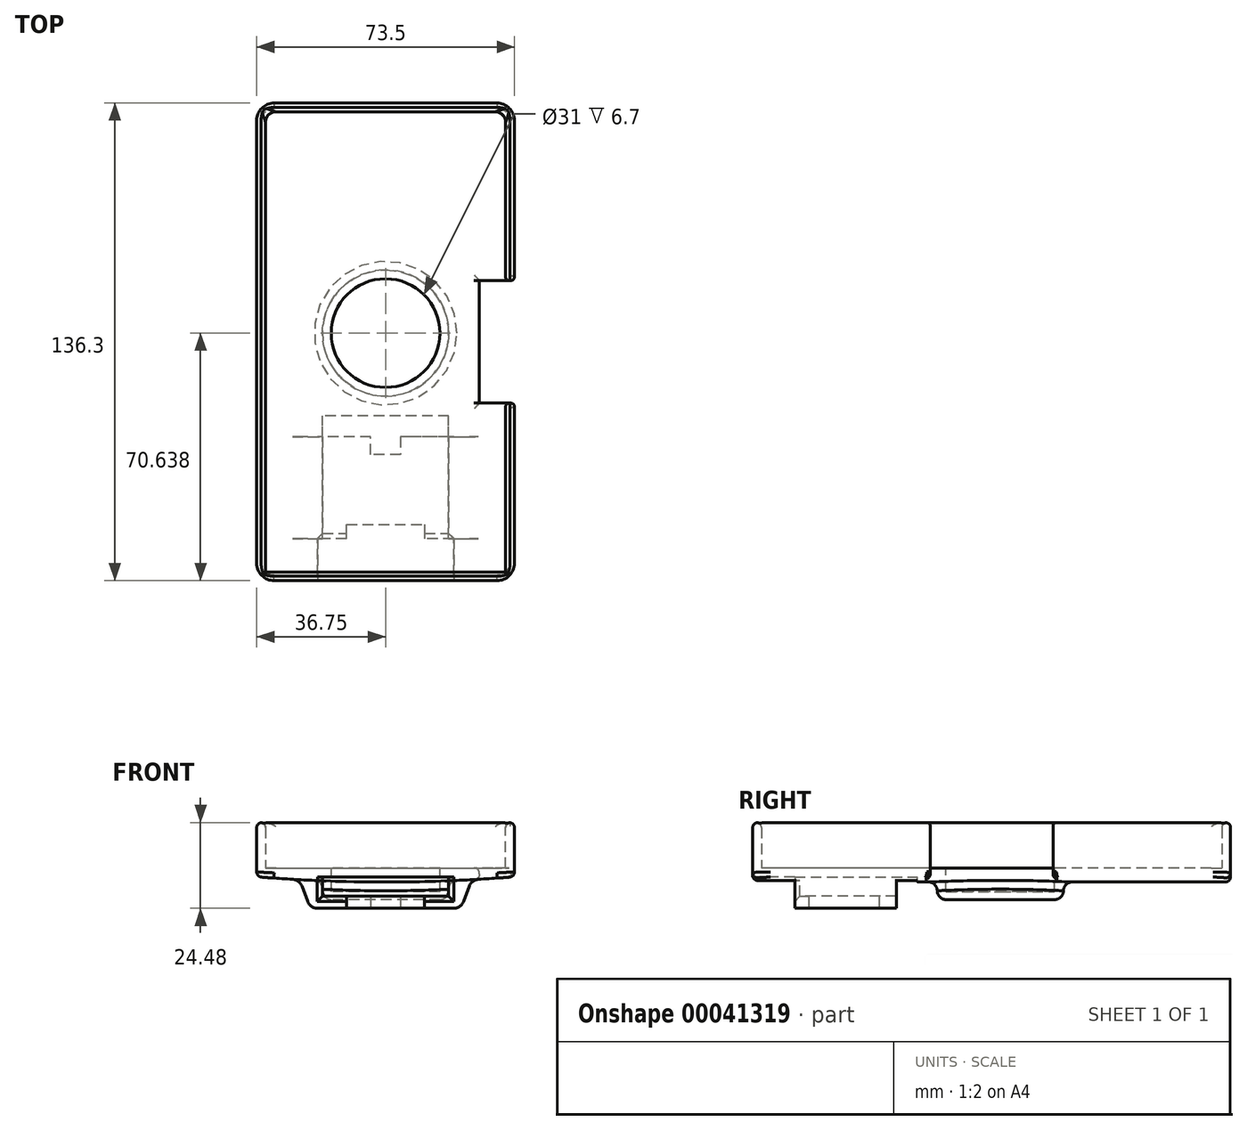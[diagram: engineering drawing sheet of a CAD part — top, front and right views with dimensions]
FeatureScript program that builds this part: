
annotation { "Feature Type Name" : "Feature", "Feature Type Description" : "" }
export const myFeature = defineFeature(function(context is Context, id is Id, definition is map)
    precondition{}
    {
        {
            var Q0;
            Q0=qCreatedBy(makeId("Top.planeOp"),FACE);
            var sketch = newSketch(context, id + "F0", { "sketchPlane" : qUnion([Q0])});
            skLineSegment(sketch, "E0.bottom", {"start": v(-33.25, 64.65) * mm, "end": v(33.25, 64.65) * mm, "construction": true});
            skLineSegment(sketch, "E0.top", {"start": v(-33.25, -64.65) * mm, "end": v(33.25, -64.65) * mm, "construction": true});
            skLineSegment(sketch, "E0.left", {"start": v(-33.25, 64.65) * mm, "end": v(-33.25, -64.65) * mm, "construction": true});
            skLineSegment(sketch, "E0.right", {"start": v(33.25, 64.65) * mm, "end": v(33.25, 14.65) * mm, "construction": true});
            skLineSegment(sketch, "E1", {"start": v(33.25, 14.65) * mm, "end": v(28.25, 14.65) * mm, "construction": true});
            skLineSegment(sketch, "E2", {"start": v(28.25, 14.65) * mm, "end": v(28.25, -14.65) * mm, "construction": true});
            skLineSegment(sketch, "E3", {"start": v(28.25, -14.65) * mm, "end": v(33.25, -14.65) * mm, "construction": true});
            skLineSegment(sketch, "E4.trimOffspring", {"start": v(33.25, -14.65) * mm, "end": v(33.25, -64.65) * mm, "construction": true});
            skCircle(sketch, "E5", {"center": v(-0.75, 2.65) * mm, "radius": 20.34 * mm, "construction": true});
            skSolve(sketch);
        }
        {
            var Q0;
            Q0=qCreatedBy(makeId("Top.planeOp"),FACE);
            var sketch = newSketch(context, id + "F1", { "sketchPlane" : qUnion([Q0])});
            skLineSegment(sketch, "E6.bottom", {"start": v(-34.25, 65.65) * mm, "end": v(34.25, 65.65) * mm, "construction": true});
            skLineSegment(sketch, "E6.top", {"start": v(-34.25, -65.65) * mm, "end": v(34.25, -65.65) * mm, "construction": true});
            skLineSegment(sketch, "E6.left", {"start": v(-34.25, 65.65) * mm, "end": v(-34.25, -65.65) * mm, "construction": true});
            skLineSegment(sketch, "E6.right", {"start": v(34.25, 65.65) * mm, "end": v(34.25, -65.65) * mm, "construction": true});
            skLineSegment(sketch, "E7.0", {"start": v(-36.75, 68.15) * mm, "end": v(36.75, 68.15) * mm});
            skLineSegment(sketch, "E7.1", {"start": v(-36.75, 68.15) * mm, "end": v(-36.75, -68.15) * mm});
            skLineSegment(sketch, "E7.2", {"start": v(-36.75, -68.15) * mm, "end": v(36.75, -68.15) * mm});
            skLineSegment(sketch, "E7.3", {"start": v(36.75, 68.15) * mm, "end": v(36.75, -68.15) * mm});
            skSolve(sketch);
        }
        {
            var Q0;
            Q0 = qSketchRegion(id + "F1", true);
            extrude(context, id + "F2", {"entities" : qUnion([Q0]), "depth" : 2.5 * mm});
        }
        {
            var Q0;
            Q0=makeQuery(id+"F2.opExtrude","CAP_FACE",FACE,{"disambiguationData":[OSD([sQuery(id+"F1.wireOp",EDGE,"E7.0"),sQuery(id+"F1.wireOp",EDGE,"E7.1"),sQuery(id+"F1.wireOp",EDGE,"E7.2"),sQuery(id+"F1.wireOp",EDGE,"E7.3")])],"isStart":false});
            var sketch = newSketch(context, id + "F3", { "sketchPlane" : qUnion([Q0])});
            skLineSegment(sketch, "E8.bottom", {"start": v(-36.75, 68.15) * mm, "end": v(36.75, 68.15) * mm});
            skLineSegment(sketch, "E8.top", {"start": v(-36.75, -68.15) * mm, "end": v(36.75, -68.15) * mm});
            skLineSegment(sketch, "E8.left", {"start": v(-36.75, 68.15) * mm, "end": v(-36.75, -68.15) * mm});
            skLineSegment(sketch, "E8.right", {"start": v(36.75, 68.15) * mm, "end": v(36.75, -68.15) * mm});
            skLineSegment(sketch, "E9.0", {"start": v(-34.25, 65.65) * mm, "end": v(34.25, 65.65) * mm});
            skLineSegment(sketch, "E9.1", {"start": v(-34.25, 65.65) * mm, "end": v(-34.25, -65.65) * mm});
            skLineSegment(sketch, "E9.2", {"start": v(-34.25, -65.65) * mm, "end": v(34.25, -65.65) * mm});
            skLineSegment(sketch, "E9.3", {"start": v(34.25, 65.65) * mm, "end": v(34.25, -65.65) * mm});
            skSolve(sketch);
        }
        {
            var Q0;
            Q0 = qSketchRegion(id + "F3", true);
            extrude(context, id + "F4", {"entities" : qUnion([Q0]), "operationType" : NewBodyOperationType.ADD, "depth" : 13 * mm});
        }
        {
            var Q0;
            Q0=makeQuery(id+"F4.boolean.opBoolean","MERGE",FACE,{"derivedFrom":[makeQuery(id+"F2.opExtrude","SWEPT_FACE",FACE,{"disambiguationData":[OSD([sQuery(id+"F1.wireOp",EDGE,"E7.0")])]}),makeQuery(id+"F4.opExtrude","SWEPT_FACE",FACE,{"disambiguationData":[OSD([sQuery(id+"F3.wireOp",EDGE,"E8.bottom")])]})]});
            var sketch = newSketch(context, id + "F5", { "sketchPlane" : qUnion([Q0])});
            skLineSegment(sketch, "E10", {"start": v(-46.23, -1.5) * mm, "end": v(62.2, -1.5) * mm, "construction": true});
            skPoint(sketch, "E11", {"position": v(0, -1.5) * mm});
            skArc(sketch, "E12", {"start": v(-36.75, 0) * mm, "mid": v(0, -1.5) * mm, "end": v(36.75, 0) * mm});
            skPoint(sketch, "E12.first.point", {"position": v(-36.75, 0) * mm});
            skPoint(sketch, "E12.second.point", {"position": v(36.75, 0) * mm});
            skLineSegment(sketch, "E13", {"start": v(36.75, 0) * mm, "end": v(-36.75, 0) * mm});
            skSolve(sketch);
        }
        {
            var Q0;
            Q0 = qSketchRegion(id + "F5", true);
            var Q1;
            Q1=makeQuery(id+"F4.boolean.opBoolean","MERGE",FACE,{"derivedFrom":[makeQuery(id+"F2.opExtrude","SWEPT_FACE",FACE,{"disambiguationData":[OSD([sQuery(id+"F1.wireOp",EDGE,"E7.2")])]}),makeQuery(id+"F4.opExtrude","SWEPT_FACE",FACE,{"disambiguationData":[OSD([sQuery(id+"F3.wireOp",EDGE,"E8.top")])]})]});
            extrude(context, id + "F6", {"entities" : qUnion([Q0]), "operationType" : NewBodyOperationType.ADD, "endBound" : BoundingType.UP_TO_SURFACE, "oppositeDirection" : true, "endBoundEntityFace" : qUnion([Q1]), "depth" : 25 * mm});
        }
        {
            var Q0;
            Q0=makeQuery(id+"F2.opExtrude","CAP_FACE",FACE,{"disambiguationData":[OSD([sQuery(id+"F1.wireOp",EDGE,"E7.0"),sQuery(id+"F1.wireOp",EDGE,"E7.1"),sQuery(id+"F1.wireOp",EDGE,"E7.2"),sQuery(id+"F1.wireOp",EDGE,"E7.3")])],"isStart":false});
            var sketch = newSketch(context, id + "F7", { "sketchPlane" : qUnion([Q0])});
            skCircle(sketch, "E14", {"center": v(0, 2.49) * mm, "radius": 15.5 * mm});
            skSolve(sketch);
        }
        {
            var Q0;
            Q0 = qSketchRegion(id + "F7", true);
            extrude(context, id + "F8", {"entities" : qUnion([Q0]), "operationType" : NewBodyOperationType.REMOVE, "endBound" : BoundingType.THROUGH_ALL, "oppositeDirection" : true, "depth" : 25 * mm});
        }
        {
            var Q0;
            Q0=qCreatedBy(makeId("Top.planeOp"),FACE);
            var sketch = newSketch(context, id + "F9", { "sketchPlane" : qUnion([Q0])});
            skCircle(sketch, "E15", {"center": v(0, 2.49) * mm, "radius": 18 * mm});
            skSolve(sketch);
        }
        {
            var Q0;
            Q0 = qSketchRegion(id + "F9", true);
            extrude(context, id + "F10", {"entities" : qUnion([Q0]), "operationType" : NewBodyOperationType.ADD, "oppositeDirection" : true, "depth" : 6.5 * mm});
        }
        {
            var Q0;
            Q0=makeQuery(id+"F2.opExtrude","CAP_FACE",FACE,{"disambiguationData":[OSD([sQuery(id+"F1.wireOp",EDGE,"E7.0"),sQuery(id+"F1.wireOp",EDGE,"E7.1"),sQuery(id+"F1.wireOp",EDGE,"E7.2"),sQuery(id+"F1.wireOp",EDGE,"E7.3")])],"isStart":false});
            var sketch = newSketch(context, id + "F11", { "sketchPlane" : qUnion([Q0])});
            skCircle(sketch, "E16", {"center": v(0, 2.49) * mm, "radius": 15.5 * mm});
            skSolve(sketch);
        }
        {
            var Q0;
            Q0 = qSketchRegion(id + "F11", true);
            extrude(context, id + "F12", {"entities" : qUnion([Q0]), "operationType" : NewBodyOperationType.REMOVE, "oppositeDirection" : true, "depth" : 6.7 * mm});
        }
        {
            var Q0;
            Q0=makeQuery(id+"F4.boolean.opBoolean","MERGE",EDGE,{"derivedFrom":[makeQuery(id+"F2.opExtrude","SWEPT_EDGE",EDGE,{"disambiguationData":[OSD([sQuery(id+"F1.wireOp",EDGE,"E7.0"),sQuery(id+"F1.wireOp",EDGE,"E7.1")])]}),makeQuery(id+"F4.opExtrude","SWEPT_EDGE",EDGE,{"disambiguationData":[OSD([sQuery(id+"F3.wireOp",EDGE,"E8.bottom"),sQuery(id+"F3.wireOp",EDGE,"E8.left")])]})]});
            var Q1;
            Q1=makeQuery(id+"F4.boolean.opBoolean","MERGE",EDGE,{"derivedFrom":[makeQuery(id+"F2.opExtrude","SWEPT_EDGE",EDGE,{"disambiguationData":[OSD([sQuery(id+"F1.wireOp",EDGE,"E7.1"),sQuery(id+"F1.wireOp",EDGE,"E7.2")])]}),makeQuery(id+"F4.opExtrude","SWEPT_EDGE",EDGE,{"disambiguationData":[OSD([sQuery(id+"F3.wireOp",EDGE,"E8.top"),sQuery(id+"F3.wireOp",EDGE,"E8.left")])]})]});
            var Q2;
            Q2=makeQuery(id+"F4.boolean.opBoolean","MERGE",EDGE,{"derivedFrom":[makeQuery(id+"F2.opExtrude","SWEPT_EDGE",EDGE,{"disambiguationData":[OSD([sQuery(id+"F1.wireOp",EDGE,"E7.2"),sQuery(id+"F1.wireOp",EDGE,"E7.3")])]}),makeQuery(id+"F4.opExtrude","SWEPT_EDGE",EDGE,{"disambiguationData":[OSD([sQuery(id+"F3.wireOp",EDGE,"E8.top"),sQuery(id+"F3.wireOp",EDGE,"E8.right")])]})]});
            var Q3;
            Q3=makeQuery(id+"F4.boolean.opBoolean","MERGE",EDGE,{"derivedFrom":[makeQuery(id+"F2.opExtrude","SWEPT_EDGE",EDGE,{"disambiguationData":[OSD([sQuery(id+"F1.wireOp",EDGE,"E7.0"),sQuery(id+"F1.wireOp",EDGE,"E7.3")])]}),makeQuery(id+"F4.opExtrude","SWEPT_EDGE",EDGE,{"disambiguationData":[OSD([sQuery(id+"F3.wireOp",EDGE,"E8.bottom"),sQuery(id+"F3.wireOp",EDGE,"E8.right")])]})]});
            fillet(context, id + "F13", {"entities" : qUnion([Q0, Q1, Q2, Q3]), "radius" : 5 * mm, "tangentPropagation" : true, "allowEdgeOverflow" : false});
        }
        {
            var Q0;
            Q0=makeQuery(id+"F2.opExtrude","CAP_FACE",FACE,{"disambiguationData":[OSD([sQuery(id+"F1.wireOp",EDGE,"E7.0"),sQuery(id+"F1.wireOp",EDGE,"E7.1"),sQuery(id+"F1.wireOp",EDGE,"E7.2"),sQuery(id+"F1.wireOp",EDGE,"E7.3")])],"isStart":false});
            var sketch = newSketch(context, id + "F14", { "sketchPlane" : qUnion([Q0])});
            skLineSegment(sketch, "E17.bottom", {"start": v(44.14, 17.5) * mm, "end": v(26.75, 17.5) * mm});
            skLineSegment(sketch, "E17.top", {"start": v(44.14, -17.5) * mm, "end": v(26.75, -17.5) * mm});
            skLineSegment(sketch, "E17.left", {"start": v(44.14, 17.5) * mm, "end": v(44.14, -17.5) * mm});
            skLineSegment(sketch, "E17.right", {"start": v(26.75, 17.5) * mm, "end": v(26.75, -17.5) * mm});
            skSolve(sketch);
        }
        {
            var Q0;
            Q0 = qSketchRegion(id + "F14", true);
            extrude(context, id + "F15", {"entities" : qUnion([Q0]), "operationType" : NewBodyOperationType.REMOVE, "oppositeDirection" : true, "depth" : 25 * mm, "hasSecondDirection" : true, "secondDirectionOppositeDirection" : false, "secondDirectionDepth" : 25 * mm});
        }
        {
            var Q0;
            Q0=qCreatedBy(makeId("Top.planeOp"),FACE);
            var sketch = newSketch(context, id + "F16", { "sketchPlane" : qUnion([Q0])});
            skLineSegment(sketch, "E18.bottom", {"start": v(18, -68.15) * mm, "end": v(-18, -68.15) * mm});
            skLineSegment(sketch, "E18.top", {"start": v(18, -21.15) * mm, "end": v(-18, -21.15) * mm});
            skLineSegment(sketch, "E18.left", {"start": v(18, -68.15) * mm, "end": v(18, -21.15) * mm});
            skLineSegment(sketch, "E18.right", {"start": v(-18, -68.15) * mm, "end": v(-18, -21.15) * mm});
            skSolve(sketch);
        }
        {
            var Q0;
            Q0 = qSketchRegion(id + "F16", true);
            extrude(context, id + "F17", {"entities" : qUnion([Q0]), "operationType" : NewBodyOperationType.REMOVE, "oppositeDirection" : true, "depth" : 25 * mm});
        }
        {
            var Q0;
            Q0=makeQuery(id+"F20.boolean.opBoolean","MERGE",FACE,{"derivedFrom":[makeQuery(id+"F6.boolean.opBoolean","MERGE",FACE,{"derivedFrom":[makeQuery(id+"F4.boolean.opBoolean","MERGE",FACE,{"derivedFrom":[makeQuery(id+"F2.opExtrude","SWEPT_FACE",FACE,{"disambiguationData":[OSD([sQuery(id+"F1.wireOp",EDGE,"E7.2")])]}),makeQuery(id+"F4.opExtrude","SWEPT_FACE",FACE,{"disambiguationData":[OSD([sQuery(id+"F3.wireOp",EDGE,"E8.top")])]})]}),makeQuery(id+"F6.opExtrude","CAP_FACE",FACE,{"disambiguationData":[OSD([sQuery(id+"F5.wireOp",EDGE,"E12"),sQuery(id+"F5.wireOp",EDGE,"E13")])],"isStart":false})]}),makeQuery(id+"F20.opExtrude","CAP_FACE",FACE,{"disambiguationData":[OSD([sQuery(id+"F19.wireOp",EDGE,"E19"),sQuery(id+"F19.wireOp",EDGE,"E20"),sQuery(id+"F19.wireOp",EDGE,"E21"),sQuery(id+"F19.wireOp",EDGE,"E22"),sQuery(id+"F19.wireOp",EDGE,"E23.MirrorCS"),sQuery(id+"F19.wireOp",EDGE,"E25.MirrorCS"),sQuery(id+"F19.wireOp",EDGE,"E26.MirrorCS"),sQuery(id+"F19.wireOp",EDGE,"E27.MirrorCS"),sQuery(id+"F19.wireOp",EDGE,"E28"),sQuery(id+"F19.wireOp",EDGE,"E29")])],"isStart":true})]});
            cPlane(context, id + "F18", {"entities" : qUnion([Q0]), "cplaneType" : CPlaneType.OFFSET, "offset" : 12 * mm, "oppositeDirection" : true, "width" : 150 * mm, "height" : 150 * mm});
        }
        {
            var Q0;
            Q0=qCreatedBy(id+"F18.planeOp",FACE);
            var sketch = newSketch(context, id + "F19", { "sketchPlane" : qUnion([Q0])});
            skLineSegment(sketch, "E19", {"start": v(18, 0) * mm, "end": v(18, -5.5) * mm});
            skLineSegment(sketch, "E20", {"start": v(18, -9) * mm, "end": v(21.5, -9) * mm});
            skLineSegment(sketch, "E21", {"start": v(21.5, -9) * mm, "end": v(24.88, 0) * mm});
            skPoint(sketch, "E21.endSnap0", {"position": v(24.88, -0.81) * mm});
            skLineSegment(sketch, "E22", {"start": v(24.88, 0) * mm, "end": v(18, 0) * mm});
            skLineSegment(sketch, "E23.MirrorCS", {"start": v(-18, 0) * mm, "end": v(-18, -5.5) * mm});
            skPoint(sketch, "E24.MirrorP", {"position": v(-24.88, -0.81) * mm});
            skLineSegment(sketch, "E25.MirrorCS", {"start": v(-18, -9) * mm, "end": v(-21.5, -9) * mm});
            skLineSegment(sketch, "E26.MirrorCS", {"start": v(-21.5, -9) * mm, "end": v(-24.88, 0) * mm});
            skLineSegment(sketch, "E27.MirrorCS", {"start": v(-24.88, 0) * mm, "end": v(-18, 0) * mm});
            skLineSegment(sketch, "E28", {"start": v(18, -9) * mm, "end": v(-18, -9) * mm});
            skLineSegment(sketch, "E29", {"start": v(18, -5.5) * mm, "end": v(-18, -5.5) * mm});
            skSolve(sketch);
        }
        {
            var Q0;
            Q0 = qSketchRegion(id + "F19", true);
            extrude(context, id + "F20", {"entities" : qUnion([Q0]), "operationType" : NewBodyOperationType.ADD, "oppositeDirection" : true, "depth" : 29 * mm});
        }
        {
            var Q0;
            Q0=makeQuery(id+"F20.opExtrude","SWEPT_FACE",FACE,{"disambiguationData":[OSD([sQuery(id+"F19.wireOp",EDGE,"E20"),sQuery(id+"F19.wireOp",EDGE,"E25.MirrorCS"),sQuery(id+"F19.wireOp",EDGE,"E28")])]});
            var sketch = newSketch(context, id + "F21", { "sketchPlane" : qUnion([Q0])});
            skLineSegment(sketch, "E30", {"start": v(-11.12, 52.15) * mm, "end": v(11.12, 52.15) * mm});
            skLineSegment(sketch, "E31", {"start": v(11.12, 56.15) * mm, "end": v(18, 56.15) * mm, "construction": true});
            skLineSegment(sketch, "E32", {"start": v(18, 56.15) * mm, "end": v(18, 27.15) * mm, "construction": true});
            skLineSegment(sketch, "E33", {"start": v(18, 27.15) * mm, "end": v(4.25, 27.15) * mm, "construction": true});
            skLineSegment(sketch, "E34", {"start": v(4.25, 32.15) * mm, "end": v(-4.25, 32.15) * mm});
            skLineSegment(sketch, "E35", {"start": v(-4.25, 27.15) * mm, "end": v(-18, 27.15) * mm, "construction": true});
            skLineSegment(sketch, "E36", {"start": v(-11.13, 56.15) * mm, "end": v(-11.13, 52.15) * mm});
            skLineSegment(sketch, "E37", {"start": v(11.12, 52.15) * mm, "end": v(11.12, 56.15) * mm});
            skLineSegment(sketch, "E38", {"start": v(4.25, 27.15) * mm, "end": v(4.25, 32.15) * mm});
            skLineSegment(sketch, "E39", {"start": v(-4.25, 32.15) * mm, "end": v(-4.25, 27.15) * mm});
            skLineSegment(sketch, "E40", {"start": v(0, 7.8) * mm, "end": v(0, 76.96) * mm, "construction": true});
            skLineSegment(sketch, "E41", {"start": v(4.25, 27.15) * mm, "end": v(-4.25, 27.15) * mm});
            skLineSegment(sketch, "E42", {"start": v(-11.13, 56.15) * mm, "end": v(11.12, 56.15) * mm});
            skSolve(sketch);
        }
        {
            var Q0;
            Q0 = qSketchRegion(id + "F21", true);
            extrude(context, id + "F22", {"entities" : qUnion([Q0]), "operationType" : NewBodyOperationType.REMOVE, "endBound" : BoundingType.UP_TO_NEXT, "oppositeDirection" : true, "depth" : 25 * mm});
        }
        {
            var Q0;
            Q0=makeQuery(id+"F4.opExtrude","CAP_EDGE",EDGE,{"disambiguationData":[OSD([sQuery(id+"F3.wireOp",EDGE,"E8.left")])],"isStart":false});
            var Q1;
            Q1=makeQuery(id+"F4.opExtrude","CAP_EDGE",EDGE,{"disambiguationData":[OSD([sQuery(id+"F3.wireOp",EDGE,"E8.bottom")])],"isStart":false});
            var Q2;
            {var subQ0=sQuery(id+"F3.wireOp",EDGE,"E8.right");Q2=makeQuery(id+"F15.boolean.opBoolean","SPLIT",EDGE,{"disambiguationData":[TD([makeQuery(id+"F15.opExtrude","SWEPT_FACE",FACE,{"disambiguationData":[OSD([sQuery(id+"F14.wireOp",EDGE,"E17.bottom")])]})])],"derivedFrom":makeQuery(id+"F4.opExtrude","CAP_EDGE",EDGE,{"disambiguationData":[OSD([subQ0])],"isStart":false})});}
            var Q3;
            {var subQ0=sQuery(id+"F3.wireOp",EDGE,"E8.right");Q3=makeQuery(id+"F15.boolean.opBoolean","SPLIT",EDGE,{"disambiguationData":[TD([makeQuery(id+"F15.opExtrude","SWEPT_FACE",FACE,{"disambiguationData":[OSD([sQuery(id+"F14.wireOp",EDGE,"E17.top")])]})])],"derivedFrom":makeQuery(id+"F4.opExtrude","CAP_EDGE",EDGE,{"disambiguationData":[OSD([subQ0])],"isStart":false})});}
            var Q4;
            Q4=makeQuery(id+"F4.opExtrude","CAP_EDGE",EDGE,{"disambiguationData":[OSD([sQuery(id+"F3.wireOp",EDGE,"E8.top")])],"isStart":false});
            var Q5;
            Q5=makeQuery(id+"F4.opExtrude","CAP_EDGE",EDGE,{"disambiguationData":[OSD([sQuery(id+"F3.wireOp",EDGE,"E9.2")])],"isStart":false});
            var Q6;
            Q6=makeQuery(id+"F4.opExtrude","CAP_EDGE",EDGE,{"disambiguationData":[OSD([sQuery(id+"F3.wireOp",EDGE,"E9.1")])],"isStart":false});
            var Q7;
            {var subQ0=sQuery(id+"F3.wireOp",EDGE,"E9.3");var subQ1=sQuery(id+"F3.wireOp",EDGE,"E9.2");Q7=makeQuery(id+"F15.boolean.opBoolean","SPLIT",EDGE,{"disambiguationData":[TD([makeQuery(id+"F4.opExtrude","SWEPT_FACE",FACE,{"disambiguationData":[OSD([subQ1])]})])],"derivedFrom":makeQuery(id+"F4.opExtrude","CAP_EDGE",EDGE,{"disambiguationData":[OSD([subQ0])],"isStart":false})});}
            var Q8;
            {var subQ0=sQuery(id+"F3.wireOp",EDGE,"E9.3");var subQ1=sQuery(id+"F3.wireOp",EDGE,"E9.0");Q8=makeQuery(id+"F15.boolean.opBoolean","SPLIT",EDGE,{"disambiguationData":[TD([makeQuery(id+"F4.opExtrude","SWEPT_FACE",FACE,{"disambiguationData":[OSD([subQ1])]})])],"derivedFrom":makeQuery(id+"F4.opExtrude","CAP_EDGE",EDGE,{"disambiguationData":[OSD([subQ0])],"isStart":false})});}
            var Q9;
            Q9=makeQuery(id+"F4.opExtrude","CAP_EDGE",EDGE,{"disambiguationData":[OSD([sQuery(id+"F3.wireOp",EDGE,"E9.0")])],"isStart":false});
            fillet(context, id + "F23", {"entities" : qUnion([Q0, Q1, Q2, Q3, Q4, Q5, Q6, Q7, Q8, Q9]), "radius" : 1.5 * mm, "tangentPropagation" : true, "allowEdgeOverflow" : false});
        }
        {
            var Q0;
            Q0=makeQuery(id+"F4.opExtrude","SWEPT_EDGE",EDGE,{"disambiguationData":[OSD([sQuery(id+"F3.wireOp",EDGE,"E9.0"),sQuery(id+"F3.wireOp",EDGE,"E9.1")])]});
            var Q1;
            Q1=makeQuery(id+"F4.opExtrude","CAP_EDGE",EDGE,{"disambiguationData":[OSD([sQuery(id+"F3.wireOp",EDGE,"E9.0")])],"isStart":true});
            var Q2;
            Q2=makeQuery(id+"F4.opExtrude","SWEPT_EDGE",EDGE,{"disambiguationData":[OSD([sQuery(id+"F3.wireOp",EDGE,"E9.0"),sQuery(id+"F3.wireOp",EDGE,"E9.3")])]});
            var Q3;
            {var subQ0=sQuery(id+"F3.wireOp",EDGE,"E9.3");Q3=makeQuery(id+"F15.boolean.opBoolean","SPLIT",EDGE,{"disambiguationData":[TD([makeQuery(id+"F4.opExtrude","SWEPT_FACE",FACE,{"disambiguationData":[OSD([sQuery(id+"F3.wireOp",EDGE,"E9.0")])]})])],"derivedFrom":makeQuery(id+"F4.opExtrude","CAP_EDGE",EDGE,{"disambiguationData":[OSD([subQ0])],"isStart":true})});}
            var Q4;
            {var subQ0=sQuery(id+"F3.wireOp",EDGE,"E9.3");Q4=makeQuery(id+"F15.boolean.opBoolean","SPLIT",EDGE,{"disambiguationData":[TD([makeQuery(id+"F4.opExtrude","SWEPT_FACE",FACE,{"disambiguationData":[OSD([sQuery(id+"F3.wireOp",EDGE,"E9.2")])]})])],"derivedFrom":makeQuery(id+"F4.opExtrude","CAP_EDGE",EDGE,{"disambiguationData":[OSD([subQ0])],"isStart":true})});}
            var Q5;
            Q5=makeQuery(id+"F4.opExtrude","CAP_EDGE",EDGE,{"disambiguationData":[OSD([sQuery(id+"F3.wireOp",EDGE,"E9.1")])],"isStart":true});
            var Q6;
            Q6=makeQuery(id+"F4.opExtrude","CAP_EDGE",EDGE,{"disambiguationData":[OSD([sQuery(id+"F3.wireOp",EDGE,"E9.2")])],"isStart":true});
            fillet(context, id + "F24", {"entities" : qUnion([Q0, Q1, Q2, Q3, Q4, Q5, Q6]), "radius" : 3 * mm, "tangentPropagation" : true, "allowEdgeOverflow" : false});
        }
        {
            var Q0;
            Q0=makeQuery(id+"F15.boolean.opBoolean","INTERSECT",EDGE,{"derivedFrom":[makeQuery(id+"F4.boolean.opBoolean","MERGE",FACE,{"derivedFrom":[makeQuery(id+"F2.opExtrude","SWEPT_FACE",FACE,{"disambiguationData":[OSD([sQuery(id+"F1.wireOp",EDGE,"E7.3")])]}),makeQuery(id+"F4.opExtrude","SWEPT_FACE",FACE,{"disambiguationData":[OSD([sQuery(id+"F3.wireOp",EDGE,"E8.right")])]})]}),makeQuery(id+"F15.opExtrude","SWEPT_FACE",FACE,{"disambiguationData":[OSD([sQuery(id+"F14.wireOp",EDGE,"E17.bottom")])]})]});
            var Q1;
            Q1=makeQuery(id+"F15.boolean.opBoolean","INTERSECT",EDGE,{"derivedFrom":[makeQuery(id+"F4.opExtrude","SWEPT_FACE",FACE,{"disambiguationData":[OSD([sQuery(id+"F3.wireOp",EDGE,"E9.3")])]}),makeQuery(id+"F15.opExtrude","SWEPT_FACE",FACE,{"disambiguationData":[OSD([sQuery(id+"F14.wireOp",EDGE,"E17.bottom")])]})]});
            var Q2;
            Q2=makeQuery(id+"F15.boolean.opBoolean","INTERSECT",EDGE,{"derivedFrom":[makeQuery(id+"F4.opExtrude","SWEPT_FACE",FACE,{"disambiguationData":[OSD([sQuery(id+"F3.wireOp",EDGE,"E9.3")])]}),makeQuery(id+"F15.opExtrude","SWEPT_FACE",FACE,{"disambiguationData":[OSD([sQuery(id+"F14.wireOp",EDGE,"E17.top")])]})]});
            var Q3;
            Q3=makeQuery(id+"F15.boolean.opBoolean","INTERSECT",EDGE,{"derivedFrom":[makeQuery(id+"F4.boolean.opBoolean","MERGE",FACE,{"derivedFrom":[makeQuery(id+"F2.opExtrude","SWEPT_FACE",FACE,{"disambiguationData":[OSD([sQuery(id+"F1.wireOp",EDGE,"E7.3")])]}),makeQuery(id+"F4.opExtrude","SWEPT_FACE",FACE,{"disambiguationData":[OSD([sQuery(id+"F3.wireOp",EDGE,"E8.right")])]})]}),makeQuery(id+"F15.opExtrude","SWEPT_FACE",FACE,{"disambiguationData":[OSD([sQuery(id+"F14.wireOp",EDGE,"E17.top")])]})]});
            fillet(context, id + "F25", {"entities" : qUnion([Q0, Q1, Q2, Q3]), "radius" : 1 * mm, "tangentPropagation" : true, "allowEdgeOverflow" : false});
        }
        {
            var Q0;
            Q0=makeQuery(id+"F15.boolean.opBoolean","INTERSECT",EDGE,{"derivedFrom":[makeQuery(id+"F2.opExtrude","CAP_FACE",FACE,{"disambiguationData":[OSD([sQuery(id+"F1.wireOp",EDGE,"E7.0"),sQuery(id+"F1.wireOp",EDGE,"E7.1"),sQuery(id+"F1.wireOp",EDGE,"E7.2"),sQuery(id+"F1.wireOp",EDGE,"E7.3")])],"isStart":false}),makeQuery(id+"F15.opExtrude","SWEPT_FACE",FACE,{"disambiguationData":[OSD([sQuery(id+"F14.wireOp",EDGE,"E17.right")])]})]});
            var Q1;
            Q1=makeQuery(id+"F15.boolean.opBoolean","INTERSECT",EDGE,{"derivedFrom":[makeQuery(id+"F6.opExtrude","SWEPT_FACE",FACE,{"disambiguationData":[OSD([sQuery(id+"F5.wireOp",EDGE,"E12")])]}),makeQuery(id+"F15.opExtrude","SWEPT_FACE",FACE,{"disambiguationData":[OSD([sQuery(id+"F14.wireOp",EDGE,"E17.right")])]})]});
            fillet(context, id + "F26", {"entities" : qUnion([Q0, Q1]), "radius" : 1.5 * mm, "tangentPropagation" : true, "allowEdgeOverflow" : false});
        }
        {
            var Q0;
            {var subQ0=sQuery(id+"F1.wireOp",EDGE,"E7.3");var subQ1=sQuery(id+"F1.wireOp",EDGE,"E7.0");var subQ2=sQuery(id+"F3.wireOp",EDGE,"E8.bottom");var subQ3=sQuery(id+"F3.wireOp",EDGE,"E8.right");var subQ4=sQuery(id+"F5.wireOp",EDGE,"E12");Q0=makeQuery(id+"F15.boolean.opBoolean","SPLIT",EDGE,{"disambiguationData":[TD([makeQuery(id+"F15.opExtrude","SWEPT_FACE",FACE,{"disambiguationData":[OSD([sQuery(id+"F14.wireOp",EDGE,"E17.bottom")])]})])],"derivedFrom":makeQuery(id+"F6.boolean.opBoolean","MERGE",EDGE,{"derivedFrom":[makeQuery(id+"F2.opExtrude","CAP_EDGE",EDGE,{"disambiguationData":[OSD([subQ0])],"isStart":true}),makeQuery(id+"F6.opExtrude","SWEPT_EDGE",EDGE,{"disambiguationData":[OSD([subQ1,subQ0,subQ2,subQ3,subQ4,sQuery(id+"F5.wireOp",EDGE,"E13")])]})]})});}
            var Q1;
            Q1=makeQuery(id+"F15.boolean.opBoolean","INTERSECT",EDGE,{"derivedFrom":[makeQuery(id+"F6.opExtrude","SWEPT_FACE",FACE,{"disambiguationData":[OSD([sQuery(id+"F5.wireOp",EDGE,"E12")])]}),makeQuery(id+"F15.opExtrude","SWEPT_FACE",FACE,{"disambiguationData":[OSD([sQuery(id+"F14.wireOp",EDGE,"E17.bottom")])]})]});
            var Q2;
            Q2=makeQuery(id+"F6.opExtrude","CAP_EDGE",EDGE,{"disambiguationData":[OSD([sQuery(id+"F5.wireOp",EDGE,"E12")])],"isStart":true});
            var Q3;
            {var subQ0=sQuery(id+"F1.wireOp",EDGE,"E7.1");Q3=makeQuery(id+"F6.boolean.opBoolean","MERGE",EDGE,{"derivedFrom":[makeQuery(id+"F2.opExtrude","CAP_EDGE",EDGE,{"disambiguationData":[OSD([subQ0])],"isStart":true}),makeQuery(id+"F6.opExtrude","SWEPT_EDGE",EDGE,{"disambiguationData":[OSD([sQuery(id+"F1.wireOp",EDGE,"E7.0"),subQ0,sQuery(id+"F3.wireOp",EDGE,"E8.bottom"),sQuery(id+"F3.wireOp",EDGE,"E8.left"),sQuery(id+"F5.wireOp",EDGE,"E12"),sQuery(id+"F5.wireOp",EDGE,"E13")])]})]});}
            var Q4;
            {var subQ0=sQuery(id+"F1.wireOp",EDGE,"E7.3");var subQ1=sQuery(id+"F3.wireOp",EDGE,"E8.right");var subQ2=sQuery(id+"F5.wireOp",EDGE,"E12");Q4=makeQuery(id+"F15.boolean.opBoolean","SPLIT",EDGE,{"disambiguationData":[TD([makeQuery(id+"F15.opExtrude","SWEPT_FACE",FACE,{"disambiguationData":[OSD([sQuery(id+"F14.wireOp",EDGE,"E17.top")])]})])],"derivedFrom":makeQuery(id+"F6.boolean.opBoolean","MERGE",EDGE,{"derivedFrom":[makeQuery(id+"F2.opExtrude","CAP_EDGE",EDGE,{"disambiguationData":[OSD([subQ0])],"isStart":true}),makeQuery(id+"F6.opExtrude","SWEPT_EDGE",EDGE,{"disambiguationData":[OSD([sQuery(id+"F1.wireOp",EDGE,"E7.0"),subQ0,sQuery(id+"F3.wireOp",EDGE,"E8.bottom"),subQ1,subQ2,sQuery(id+"F5.wireOp",EDGE,"E13")])]})]})});}
            var Q5;
            {var subQ0=sQuery(id+"F5.wireOp",EDGE,"E12");Q5=makeQuery(id+"F17.boolean.opBoolean","SPLIT",EDGE,{"disambiguationData":[TD([makeQuery(id+"F17.opExtrude","SWEPT_FACE",FACE,{"disambiguationData":[OSD([sQuery(id+"F16.wireOp",EDGE,"E18.left")])]})])],"derivedFrom":makeQuery(id+"F6.opExtrude","CAP_EDGE",EDGE,{"disambiguationData":[OSD([subQ0])],"isStart":false})});}
            var Q6;
            {var subQ0=sQuery(id+"F5.wireOp",EDGE,"E12");Q6=makeQuery(id+"F17.boolean.opBoolean","SPLIT",EDGE,{"disambiguationData":[TD([makeQuery(id+"F17.opExtrude","SWEPT_FACE",FACE,{"disambiguationData":[OSD([sQuery(id+"F16.wireOp",EDGE,"E18.right")])]})])],"derivedFrom":makeQuery(id+"F6.opExtrude","CAP_EDGE",EDGE,{"disambiguationData":[OSD([subQ0])],"isStart":false})});}
            fillet(context, id + "F27", {"entities" : qUnion([Q0, Q1, Q2, Q3, Q4, Q5, Q6]), "radius" : 1.5 * mm, "tangentPropagation" : true, "allowEdgeOverflow" : false});
        }
        {
            var Q0;
            Q0=makeQuery(id+"F10.boolean.opBoolean","INTERSECT",EDGE,{"derivedFrom":[makeQuery(id+"F6.opExtrude","SWEPT_FACE",FACE,{"disambiguationData":[OSD([sQuery(id+"F5.wireOp",EDGE,"E12")])]}),makeQuery(id+"F10.opExtrude","SWEPT_FACE",FACE,{"disambiguationData":[OSD([sQuery(id+"F9.wireOp",EDGE,"E15")])]})]});
            var Q1;
            Q1=makeQuery(id+"F10.opExtrude","CAP_EDGE",EDGE,{"disambiguationData":[OSD([sQuery(id+"F9.wireOp",EDGE,"E15")])],"isStart":false});
            fillet(context, id + "F28", {"entities" : qUnion([Q0, Q1]), "radius" : 2.5 * mm, "tangentPropagation" : true, "allowEdgeOverflow" : false});
        }
        {
            var Q0;
            Q0=makeQuery(id+"F22.boolean.opBoolean","COPY",EDGE,{"derivedFrom":makeQuery(id+"F22.opExtrude","CAP_EDGE",EDGE,{"disambiguationData":[OSD([sQuery(id+"F21.wireOp",EDGE,"E30")])],"isStart":false})});
            var Q1;
            {var subQ1=sQuery(id+"F19.wireOp",EDGE,"E29");Q1=makeQuery(id+"F22.boolean.opBoolean","SPLIT",EDGE,{"disambiguationData":[TD([makeQuery(id+"F17.boolean.opBoolean","COPY",FACE,{"derivedFrom":makeQuery(id+"F17.opExtrude","SWEPT_FACE",FACE,{"disambiguationData":[OSD([sQuery(id+"F16.wireOp",EDGE,"E18.right")])]})})])],"derivedFrom":makeQuery(id+"F20.opExtrude","CAP_EDGE",EDGE,{"disambiguationData":[OSD([subQ1])],"isStart":true})});}
            var Q2;
            {var subQ0=sQuery(id+"F19.wireOp",EDGE,"E29");Q2=makeQuery(id+"F22.boolean.opBoolean","SPLIT",EDGE,{"disambiguationData":[TD([makeQuery(id+"F17.boolean.opBoolean","COPY",FACE,{"derivedFrom":makeQuery(id+"F17.opExtrude","SWEPT_FACE",FACE,{"disambiguationData":[OSD([sQuery(id+"F16.wireOp",EDGE,"E18.left")])]})})])],"derivedFrom":makeQuery(id+"F20.opExtrude","CAP_EDGE",EDGE,{"disambiguationData":[OSD([subQ0])],"isStart":true})});}
            var Q3;
            Q3=makeQuery(id+"F20.opExtrude","CAP_EDGE",EDGE,{"disambiguationData":[OSD([sQuery(id+"F19.wireOp",EDGE,"E19")])],"isStart":true});
            var Q4;
            Q4=makeQuery(id+"F20.opExtrude","CAP_EDGE",EDGE,{"disambiguationData":[OSD([sQuery(id+"F19.wireOp",EDGE,"E23.MirrorCS")])],"isStart":true});
            chamfer(context, id + "F29", {"entities" : qUnion([Q0, Q1, Q2, Q3, Q4]), "width" : 1.5 * mm, "tangentPropagation" : true});
        }
        {
            var Q0;
            Q0=makeQuery(id+"F20.opExtrude","SWEPT_EDGE",EDGE,{"disambiguationData":[OSD([sQuery(id+"F19.wireOp",EDGE,"E20"),sQuery(id+"F19.wireOp",EDGE,"E21")])]});
            var Q1;
            Q1=makeQuery(id+"F20.boolean.opBoolean","INTERSECT",EDGE,{"derivedFrom":[makeQuery(id+"F6.opExtrude","SWEPT_FACE",FACE,{"disambiguationData":[OSD([sQuery(id+"F5.wireOp",EDGE,"E12")])]}),makeQuery(id+"F20.opExtrude","SWEPT_FACE",FACE,{"disambiguationData":[OSD([sQuery(id+"F19.wireOp",EDGE,"E21")])]})]});
            var Q2;
            Q2=makeQuery(id+"F20.opExtrude","SWEPT_EDGE",EDGE,{"disambiguationData":[OSD([sQuery(id+"F19.wireOp",EDGE,"E25.MirrorCS"),sQuery(id+"F19.wireOp",EDGE,"E26.MirrorCS")])]});
            var Q3;
            Q3=makeQuery(id+"F20.boolean.opBoolean","INTERSECT",EDGE,{"derivedFrom":[makeQuery(id+"F6.opExtrude","SWEPT_FACE",FACE,{"disambiguationData":[OSD([sQuery(id+"F5.wireOp",EDGE,"E12")])]}),makeQuery(id+"F20.opExtrude","SWEPT_FACE",FACE,{"disambiguationData":[OSD([sQuery(id+"F19.wireOp",EDGE,"E26.MirrorCS")])]})]});
            fillet(context, id + "F30", {"entities" : qUnion([Q0, Q1, Q2, Q3]), "radius" : 3 * mm, "tangentPropagation" : true, "allowEdgeOverflow" : false});
        }
        {
            var Q0;
            Q0=makeQuery(id+"F6.boolean.opBoolean","MERGE",FACE,{"derivedFrom":[makeQuery(id+"F4.boolean.opBoolean","MERGE",FACE,{"derivedFrom":[makeQuery(id+"F2.opExtrude","SWEPT_FACE",FACE,{"disambiguationData":[OSD([sQuery(id+"F1.wireOp",EDGE,"E7.2")])]}),makeQuery(id+"F4.opExtrude","SWEPT_FACE",FACE,{"disambiguationData":[OSD([sQuery(id+"F3.wireOp",EDGE,"E8.top")])]})]}),makeQuery(id+"F6.opExtrude","CAP_FACE",FACE,{"disambiguationData":[OSD([sQuery(id+"F5.wireOp",EDGE,"E12"),sQuery(id+"F5.wireOp",EDGE,"E13")])],"isStart":false})]});
            var sketch = newSketch(context, id + "F31", { "sketchPlane" : qUnion([Q0])});
            skLineSegment(sketch, "E43.bottom", {"start": v(-19.43, -3.8) * mm, "end": v(-16.53, -3.8) * mm});
            skLineSegment(sketch, "E43.top", {"start": v(-19.43, 0) * mm, "end": v(-16.53, 0) * mm});
            skLineSegment(sketch, "E43.left", {"start": v(-19.43, -3.8) * mm, "end": v(-19.43, 0) * mm});
            skLineSegment(sketch, "E43.right", {"start": v(-16.53, -3.8) * mm, "end": v(-16.53, 0) * mm});
            skLineSegment(sketch, "E44.MirrorCS", {"start": v(19.43, 0) * mm, "end": v(16.53, 0) * mm});
            skLineSegment(sketch, "E45.MirrorCS", {"start": v(19.43, -3.8) * mm, "end": v(16.53, -3.8) * mm});
            skLineSegment(sketch, "E46.MirrorCS", {"start": v(16.53, -3.8) * mm, "end": v(16.53, 0) * mm});
            skLineSegment(sketch, "E47.MirrorCS", {"start": v(19.43, -3.8) * mm, "end": v(19.43, 0) * mm});
            skSolve(sketch);
        }
        {
            var Q0;
            Q0 = qSketchRegion(id + "F31", true);
            var Q1;
            {var subQ0=sQuery(id+"F19.wireOp",EDGE,"E23.MirrorCS");var subQ1=sQuery(id+"F19.wireOp",EDGE,"E28");var subQ2=sQuery(id+"F19.wireOp",EDGE,"E25.MirrorCS");var subQ3=sQuery(id+"F19.wireOp",EDGE,"E20");var subQ4=sQuery(id+"F19.wireOp",EDGE,"E29");var subQ5=sQuery(id+"F19.wireOp",EDGE,"E26.MirrorCS");Q1=makeQuery(id+"F22.boolean.opBoolean","SPLIT",FACE,{"disambiguationData":[TD([makeQuery(id+"F17.boolean.opBoolean","COPY",FACE,{"derivedFrom":makeQuery(id+"F17.opExtrude","SWEPT_FACE",FACE,{"disambiguationData":[OSD([sQuery(id+"F16.wireOp",EDGE,"E18.right")])]})})])],"derivedFrom":makeQuery(id+"F20.opExtrude","CAP_FACE",FACE,{"disambiguationData":[OSD([sQuery(id+"F19.wireOp",EDGE,"E19"),subQ3,sQuery(id+"F19.wireOp",EDGE,"E21"),sQuery(id+"F19.wireOp",EDGE,"E22"),subQ0,subQ2,subQ5,sQuery(id+"F19.wireOp",EDGE,"E27.MirrorCS"),subQ1,subQ4])],"isStart":true})});}
            extrude(context, id + "F32", {"entities" : qUnion([Q0]), "operationType" : NewBodyOperationType.REMOVE, "endBound" : BoundingType.UP_TO_SURFACE, "oppositeDirection" : true, "endBoundEntityFace" : qUnion([Q1]), "depth" : 25 * mm});
        }
    });
